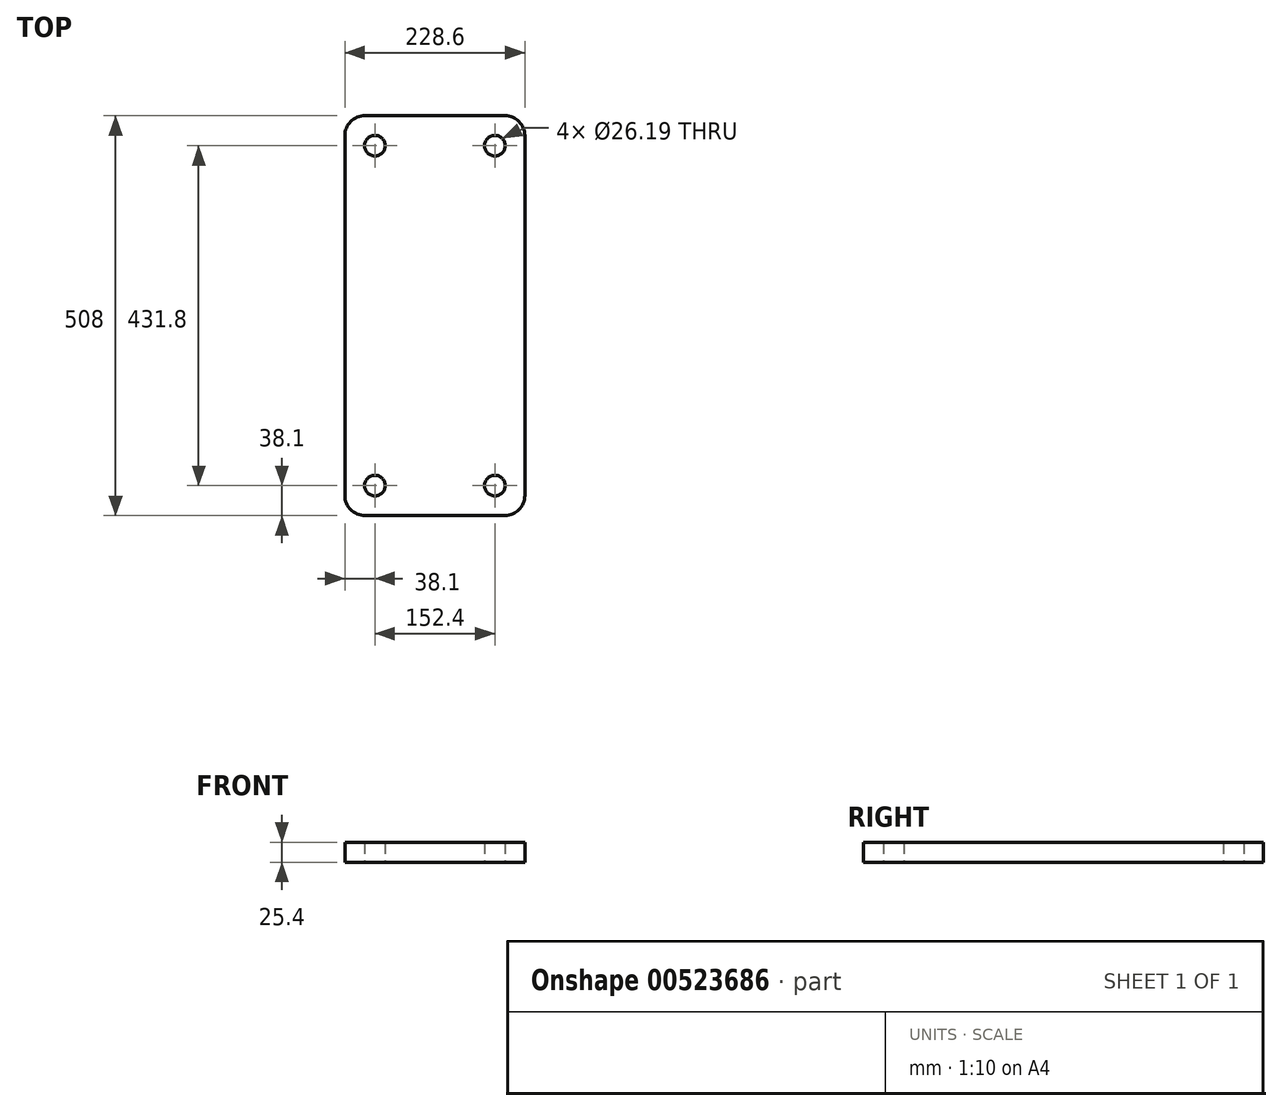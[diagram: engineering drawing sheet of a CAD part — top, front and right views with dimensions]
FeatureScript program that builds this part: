
annotation { "Feature Type Name" : "Feature", "Feature Type Description" : "" }
export const myFeature = defineFeature(function(context is Context, id is Id, definition is map)
    precondition{}
    {
        {
            var Q0;
            Q0=qCreatedBy(makeId("Top.planeOp"),FACE);
            var sketch = newSketch(context, id + "F0", { "sketchPlane" : qUnion([Q0])});
            skLineSegment(sketch, "E0.bottom", {"start": v(-88.9, 254) * mm, "end": v(88.9, 254) * mm});
            skLineSegment(sketch, "E0.top", {"start": v(-88.9, -254) * mm, "end": v(88.9, -254) * mm});
            skLineSegment(sketch, "E0.left", {"start": v(-114.3, 228.6) * mm, "end": v(-114.3, -228.6) * mm});
            skLineSegment(sketch, "E0.right", {"start": v(114.3, 228.6) * mm, "end": v(114.3, -228.6) * mm});
            skCircle(sketch, "E1", {"center": v(-76.2, 215.9) * mm, "radius": 13.1 * mm});
            skCircle(sketch, "E2", {"center": v(76.2, 215.9) * mm, "radius": 13.1 * mm});
            skCircle(sketch, "E3", {"center": v(76.2, -215.9) * mm, "radius": 13.1 * mm});
            skCircle(sketch, "E4", {"center": v(-76.2, -215.9) * mm, "radius": 13.1 * mm});
            skPoint(sketch, "E5.visualSharp", {"position": v(-114.3, 254) * mm});
            skArc(sketch, "E5.filletArc", {"start": v(-88.9, 254) * mm, "mid": v(-106.86, 246.56) * mm, "end": v(-114.3, 228.6) * mm});
            skPoint(sketch, "E6.visualSharp", {"position": v(114.3, 254) * mm});
            skArc(sketch, "E6.filletArc", {"start": v(114.3, 228.6) * mm, "mid": v(106.86, 246.56) * mm, "end": v(88.9, 254) * mm});
            skPoint(sketch, "E7.visualSharp", {"position": v(114.3, -254) * mm});
            skArc(sketch, "E7.filletArc", {"start": v(88.9, -254) * mm, "mid": v(106.86, -246.56) * mm, "end": v(114.3, -228.6) * mm});
            skPoint(sketch, "E8.visualSharp", {"position": v(-114.3, -254) * mm});
            skArc(sketch, "E8.filletArc", {"start": v(-114.3, -228.6) * mm, "mid": v(-106.86, -246.56) * mm, "end": v(-88.9, -254) * mm});
            skSolve(sketch);
        }
        {
            var Q0;
            Q0=makeQuery(id+"F0.imprint","IMPRINT",FACE,{"disambiguationData":[TD([[makeQuery(id+"F0.imprint","IMPRINT",EDGE,{"derivedFrom":sQuery(id+"F0.wireOp",EDGE,"E0.bottom")}),-1.0]])]});
            extrude(context, id + "F1", {"entities" : qUnion([Q0]), "depth" : 25.4 * mm, "offsetDistance" : 25.4 * mm});
        }
    });
